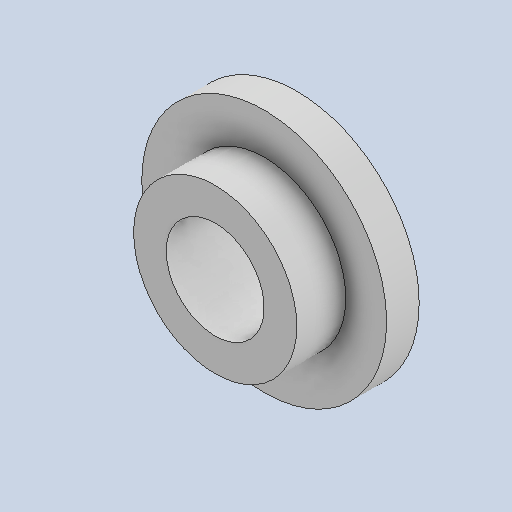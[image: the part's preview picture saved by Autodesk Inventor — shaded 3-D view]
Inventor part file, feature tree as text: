
AUTODESK INVENTOR PART (.ipt)
format: ipt  version: 2024.3 (Build 283343000, 343)  size: 262,144 bytes
history: native  units: mm
features: extrude x4, sketch x4, other x1
ambient origin geometry x8: Origin, YZ Plane, XZ Plane, XY Plane, X Axis, Y Axis, Z Axis, Center Point
bodies: Body1 (feature_tree)
feature tree (9):
  other  "ソリッド1"
  extrude  "押し出し1"  Depth=10.0mm
  extrude  "押し出し2"  Depth=15.0mm
  extrude  "押し出し4"  Depth=8.0mm TaperAngle=0.0deg
  extrude  "押し出し5"  Depth=10.0mm
  sketch  "スケッチ1"
  sketch  "スケッチ2"
  sketch  "スケッチ4"
  sketch  "スケッチ5"
